# Revit family: bfs-300_1000tua2(-50)_tu2_50Hz
name_source: partatom
category: 機械設備
units: mm (PartAtom-declared; Revit-internal decimal feet)

## family parameters
OmniClass タイトル = Centrifugal Fans
OmniClass 番号 = 23.75.35.17.27
パーツ タイプ = 割り込み
ロード時にボイドで切り取り = いいえ
丸型コネクタ寸法 = 直径を使用
作業面ベース = いいえ
共有 = いいえ
常に垂直 = はい
部屋計算ポイント = はい

## types (5) — shared parameters
Clearance Left = 450
IfcExportAs = IfcFanType
IfcExportType = CENTRIFUGALFORWARDCURVED
MID静圧 = 0.0 Pa
MID風量 = 0.0 m³/h
MIN静圧 = 0.0 Pa
MIN風量 = 0.0 m³/h
OmniClassCode = 23-33 31 19 13 15
URL = https://www.mitsubishielectric.co.jp
Uniclass2015Code = Pr_65_67_29_12
Uniclass2015Title = Centrifugal fans
Uniclass2015Version = Systems v1.9
サービススペース = はい
ファンの種類 = 多翼形
仕様書バージョン = Version1.0
企業コード = 108420
分類コード = 50052502100020
周波数 = 50 Hz
呼称 = 消音ボックス付送風機
実風量 = 0.0 m³/h
形名 = BFS-TUA : BFS-300TUA
本体マテリアル = 溶融亜鉛めっき鋼板
極 = 4
極数 = 3
法定耐用年数 = 15
盤工事区分 = 電気工事
相 = 3
積算_科目 = 2 換気設備
製品リリース年月 = 2022年6月1日
製品出荷対象 = 国内
製造元 = 三菱電機株式会社
設置方法 = 天吊
説明 = ストレートシロッコファン天吊埋込タイプ（消音形）
負荷分類 = 3_ファン類
運転質量 = 0.00 kg
電圧 = 200 V
zero-valued in all types: Clearance Back, Clearance Bottom, Clearance Front, Clearance Right, Clearance Top

## per-type parameters (varying)
| type | Depth | Height | M | MAX静圧 | MAX風量 | Width | ダクト幅 | ダクト高 | 価格 | 参照している仕様書等のバージョン | 天吊金具ピッチ奥行 | 天吊金具ピッチ幅 | 消費電力 | 点検口位置 | 番手 | 製品質量 | 質量 | 電動機出力 | 騒音レベル(dB(A)) | 騒音レベル(dB(A))_側面 | 騒音レベル(dB(A))_吐出 | 騒音レベル(dB(A))_吸込 |
| BFS-300TUA2-50 | 977  [stored 3.20538 ft] | 413  [stored 1.35499 ft] | 79 | 220.0 Pa | 3000.0 m³/h | 586  [stored 1.92257 ft] | 300 mm | 300 mm | 320000 $ |  | 924  [stored 3.0315 ft] | 695  [stored 2.28018 ft] | 910 W | 80  [stored 0.262467 ft] | #2 | 44.00 kg | 52.80 kg | 1000 W | 73 | 44 | 73 | 49 |
| BFS-450TUA2 | 1010  [stored 3.31365 ft] | 373  [stored 1.22375 ft] | 79 | 190.0 Pa | 4500.0 m³/h | 884  [stored 2.90026 ft] | 700 mm | 250 mm | 516000 $ | 公共建築工事標準仕様書（機械設備工事編）平成31年度版 | 962  [stored 3.15617 ft] | 989  [stored 3.24475 ft] | 1150 W | 282.5 | #1 1/2×2 | 78.00 kg | 93.60 kg | 2200 W | 71 | 43 | 71 | 52 |
| BFS-550TUA2-50 | 1078  [stored 3.53675 ft] | 413  [stored 1.35499 ft] | 79 | 200.0 Pa | 5500.0 m³/h | 1020  [stored 3.34646 ft] | 750 mm | 300 mm | 574000 $ |  | 1033  [stored 3.38911 ft] | 1124  [stored 3.68766 ft] | 1750 W | 282 | #2×2 | 90.00 kg | 108.00 kg | 2000 W | 71 | 45 | 71 | 54 |
| BFS-800TU2 | 1682 | 433  [stored 1.4206 ft] | 80  [stored 0.262467 ft] | 200.0 Pa | 8000.0 m³/h | 950  [stored 3.1168 ft] | 800 mm | 300 mm | 1100000 $ |  | 1630  [stored 5.34777 ft] | 1061  [stored 3.48097 ft] | 2700 W | 281 | #2×3 | 120.00 kg | 144.00 kg | 3500 W | 69 | 44.5 | 69 | 60.5 |
| BFS-1000TU2 | 1902  [stored 6.24016 ft] | 433  [stored 1.4206 ft] | 80  [stored 0.262467 ft] | 205.0 Pa | 10000.0 m³/h | 1070  [stored 3.5105 ft] | 900 mm | 300 mm | 1169000 $ |  | 1850  [stored 6.06955 ft] | 1181  [stored 3.87467 ft] | 3500 W | 281 | #2×4 | 150.00 kg | 180.00 kg | 4400 W | 69.5 | 45 | 69.5 | 61 |

note: column(s) folded — value = type name in every type: モデル

note: [stored X ft] marks values corroborated as IEEE doubles in the binary element streams (Revit-internal decimal feet)
